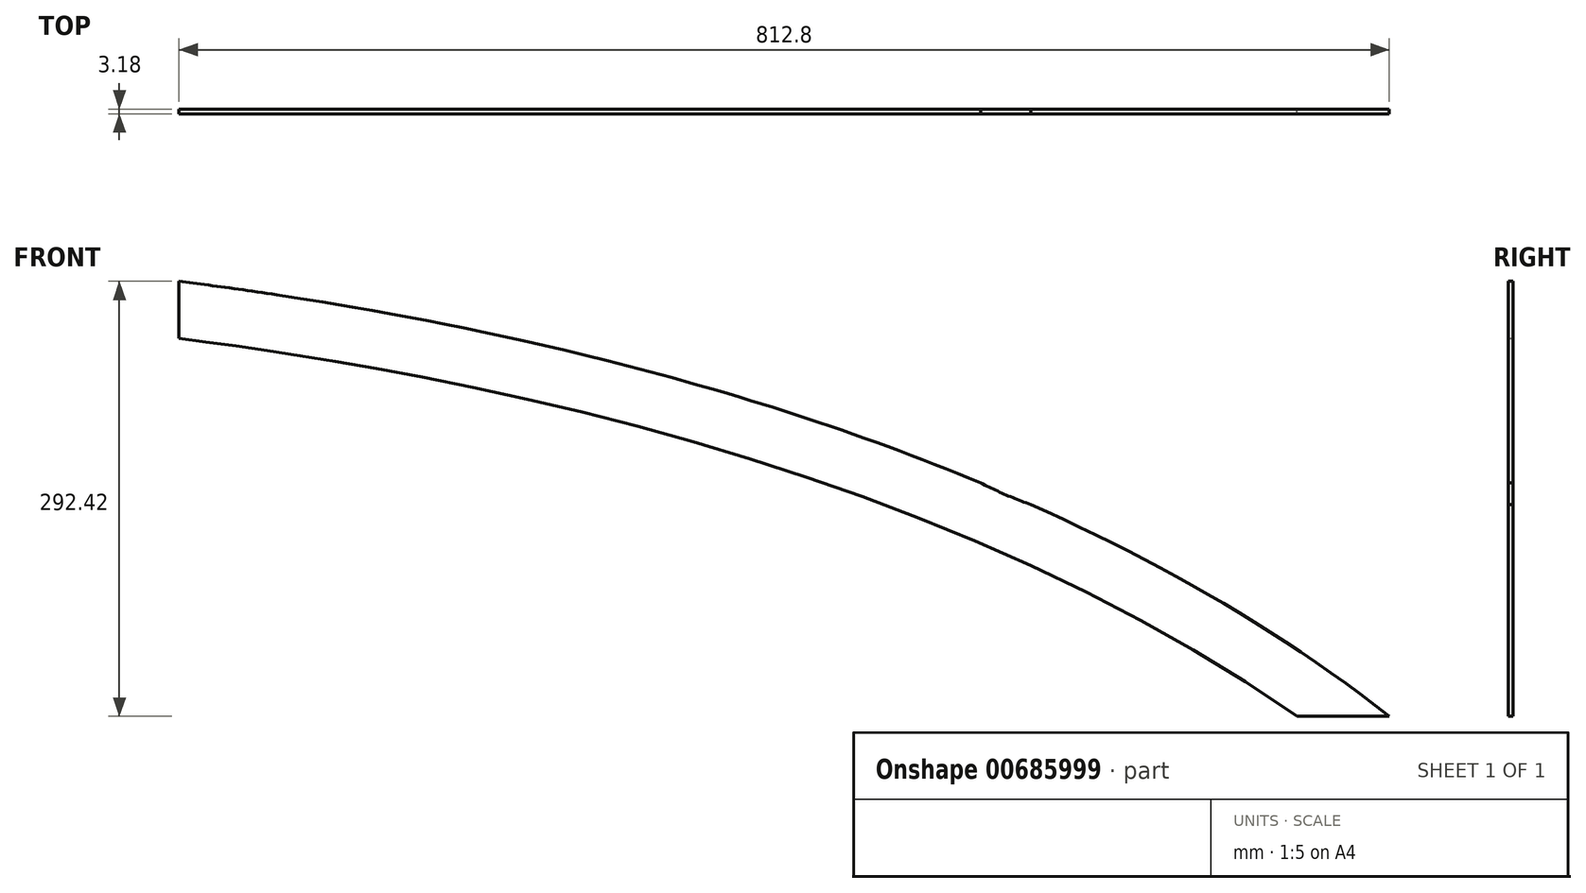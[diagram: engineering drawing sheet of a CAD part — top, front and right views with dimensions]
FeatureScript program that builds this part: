
annotation { "Feature Type Name" : "Feature", "Feature Type Description" : "" }
export const myFeature = defineFeature(function(context is Context, id is Id, definition is map)
    precondition{}
    {
        {
            var Q0;
            Q0=qCreatedBy(makeId("Front.planeOp"),FACE);
            var sketch = newSketch(context, id + "F0", { "sketchPlane" : qUnion([Q0])});
            skPoint(sketch, "E0.middle", {"position": v(0, 0) * mm});
            skPoint(sketch, "E1.0.1.0", {"position": v(0, -38.1) * mm});
            skPoint(sketch, "E1.1.0.0", {"position": v(-25.4, 0) * mm});
            skPoint(sketch, "E1.1.1.0", {"position": v(-25.4, -38.1) * mm});
            skPoint(sketch, "E0.bottom.end.orphan", {"position": v(-406.4, -127) * mm});
            skPoint(sketch, "E0.top.start.orphan", {"position": v(406.4, 127) * mm});
            skFitSpline(sketch, "E2.0", {"points": [v(-473.03, 145.88) * mm, v(-472.28, 145.7) * mm, v(-470.91, 145.42) * mm, v(-468.99, 145.05) * mm, v(-467.08, 144.72) * mm, v(-464.46, 144.3) * mm, v(-460.95, 143.77) * mm, v(-456.22, 143.11) * mm, v(-450.9, 142.4) * mm, v(-444.96, 141.64) * mm, v(-438.42, 140.8) * mm, v(-428.87, 139.57) * mm, v(-415.41, 137.82) * mm, v(-396.95, 135.32) * mm, v(-376.28, 132.39) * mm, v(-353.55, 128.96) * mm, v(-328.88, 125) * mm, v(-293.61, 118.97) * mm, v(-245.41, 109.87) * mm, v(-182.15, 96.12) * mm, v(-114.62, 79.2) * mm, v(-44, 58.77) * mm, v(28.53, 34.5) * mm, v(101.8, 6.07) * mm, v(174.63, -26.84) * mm, v(245.85, -64.52) * mm, v(314.3, -107.26) * mm, v(378.86, -155.3) * mm, v(418.57, -191.07) * mm, v(437.42, -209.92) * mm]});
            skLineSegment(sketch, "E3", {"start": v(0, -114.88) * mm, "end": v(0, -6.93) * mm});
            skLineSegment(sketch, "E4", {"start": v(-38.1, -114.88) * mm, "end": v(-38.1, 32.3) * mm});
            skLineSegment(sketch, "E5", {"start": v(0, -114.88) * mm, "end": v(-38.1, -114.88) * mm});
            skLineSegment(sketch, "E6", {"start": v(-38.1, -114.88) * mm, "end": v(0, -114.88) * mm});
            skLineSegment(sketch, "E7", {"start": v(387.35, -114.88) * mm, "end": v(323.4, -114.88) * mm});
            skLineSegment(sketch, "E8", {"start": v(-425.45, 139.12) * mm, "end": v(-425.45, 173.9) * mm});
            skLineSegment(sketch, "E9", {"start": v(-425.45, 177.54) * mm, "end": v(-425.45, 173.9) * mm});
            skPoint(sketch, "E10.orphan", {"position": v(-425.45, 474.65) * mm});
            skPoint(sketch, "E11.orphan", {"position": v(-425.45, -114.88) * mm});
            skLineSegment(sketch, "E12.trimOffspring", {"start": v(323.4, -114.88) * mm, "end": v(387.35, -114.88) * mm});
            skFitSpline(sketch, "E13.trimOffspring", {"points": [v(-473.03, 145.88) * mm, v(-472.28, 145.7) * mm, v(-470.91, 145.42) * mm, v(-468.99, 145.05) * mm, v(-467.08, 144.72) * mm, v(-464.46, 144.3) * mm, v(-460.95, 143.77) * mm, v(-456.22, 143.11) * mm, v(-450.9, 142.4) * mm, v(-444.96, 141.64) * mm, v(-438.42, 140.8) * mm, v(-428.87, 139.57) * mm, v(-415.41, 137.82) * mm, v(-396.95, 135.32) * mm, v(-376.28, 132.39) * mm, v(-353.55, 128.96) * mm, v(-328.88, 125) * mm, v(-293.61, 118.97) * mm, v(-245.41, 109.87) * mm, v(-182.15, 96.12) * mm, v(-114.62, 79.2) * mm, v(-44, 58.77) * mm, v(28.53, 34.5) * mm, v(101.8, 6.07) * mm, v(174.63, -26.84) * mm, v(245.85, -64.52) * mm, v(314.3, -107.26) * mm, v(378.86, -155.3) * mm, v(418.57, -191.07) * mm, v(437.42, -209.92) * mm]});
            skArc(sketch, "E14", {"start": v(-38.1, 32.3) * mm, "mid": v(-46.49, 49.98) * mm, "end": v(-60.75, 63.37) * mm});
            skArc(sketch, "E15", {"start": v(47.14, 27) * mm, "mid": v(15.06, 21.86) * mm, "end": v(0, -6.93) * mm});
            skPoint(sketch, "E16.orphan", {"position": v(-88.9, 71.62) * mm});
            skPoint(sketch, "E17.orphan", {"position": v(-38.1, 56.38) * mm});
            skPoint(sketch, "E18.orphan", {"position": v(0, 43.87) * mm});
            skArc(sketch, "E19", {"start": v(-88.6, 214.3) * mm, "mid": v(-264.33, 262.92) * mm, "end": v(-425.45, 177.54) * mm});
            skArc(sketch, "E20.0", {"start": v(-54.45, 117.55) * mm, "mid": v(-194.16, 221.71) * mm, "end": v(-364.17, 183.46) * mm});
            skFitSpline(sketch, "E21.trimOffspring", {"points": [v(-464.36, 182.99) * mm, v(464.36, -182.99) * mm], "startDerivative": vector(116.74, -27.26) * mm, "endDerivative": vector(950.03, -950.44) * mm});
            skFitSpline(sketch, "E22.trimOffspring", {"points": [v(-464.36, 182.99) * mm, v(464.36, -182.99) * mm], "startDerivative": vector(116.74, -27.26) * mm, "endDerivative": vector(950.03, -950.44) * mm});
            skArc(sketch, "E23", {"start": v(-64.34, 104.19) * mm, "mid": v(-56.88, 109) * mm, "end": v(-54.45, 117.55) * mm});
            skPoint(sketch, "E24.orphan", {"position": v(-45.29, 98.5) * mm});
            skPoint(sketch, "E25.orphan", {"position": v(0, 84.08) * mm});
            skArc(sketch, "E26", {"start": v(-364.17, 183.46) * mm, "mid": v(-364.56, 175.16) * mm, "end": v(-359.72, 168.41) * mm});
            skPoint(sketch, "E27.orphan", {"position": v(-378.77, 171.21) * mm});
            skPoint(sketch, "E28", {"position": v(-202.29, 261.84) * mm});
            skPoint(sketch, "E29.startDerivative.orphan", {"position": v(0, 91.29) * mm});
            skPoint(sketch, "E30.orphan", {"position": v(-38.1, 5.58) * mm});
            skFitSpline(sketch, "E31", {"points": [v(-88.6, 214.3) * mm, v(146.48, 27.46) * mm], "startDerivative": vector(234.86, -187.43) * mm, "endDerivative": vector(307.14, -108.87) * mm});
            skPoint(sketch, "E32.orphan", {"position": v(19.42, 77.49) * mm});
            skPoint(sketch, "E33.orphan", {"position": v(50.8, 25.62) * mm});
            skSolve(sketch);
        }
        {
            var Q0;
            {var subQ11=sQuery(id+"F0.wireOp",EDGE,"E2.0");Q0=makeQuery(id+"F0.imprint","IMPRINT",FACE,{"disambiguationData":[TD([[makeQuery(id+"F0.imprint","IMPRINT",EDGE,{"derivedFrom":subQ11}),1.0]])]});}
            extrude(context, id + "F1", {"entities" : qUnion([Q0]), "depth" : 3.17 * mm, "offsetDistance" : 25.4 * mm});
        }
    });
